# Revit family: Door_Coiling_UltiGroup_Spiral Plus
name_source: partatom
category: Doors
revit_build: Autodesk Revit 2018 (Build: 20170223_1515(x64)
units: mm (PartAtom-declared; Revit-internal decimal feet)

## family parameters
Always vertical = Yes
Cut with Voids When Loaded = No
Host = Wall
OmniClass Number = 23.30.10.17.27.11
OmniClass Title = Overhead Coiling
Room Calculation Point = No
Shared = No

## types (1)
- Type 1
    Analytic Construction = <None>
    Control Box Distance = 150 mm
    Control Box Height = 1200 mm
    Description = Ulti Spiral Plus Door
    Door Bottom Seal = 40 mm  [stored 0.131234 ft]
    Door Seal = Door Seal
    Door open = 0 mm  [stored 0 ft]
    DoorFrameMaterial_ANZRS = Door Frame Material
    DoorGlazingHeight_ANZRS = 0 mm  [stored 0 ft]
    DoorGlazingWidth_ANZRS = 0 mm  [stored 0 ft]
    DoorGrilleHeight_ANZRS = 0 mm  [stored 0 ft]
    DoorGrilleWidth_ANZRS = 0 mm  [stored 0 ft]
    DoorGrille_ANZRS = No
    DoorNumberOfPanels_ANZRS = 0
    DoorOperation_ANZRS = Large heavy duty mushroom head push button, push button and emergency stop button fitted to control box
    DoorPanelBWidth_ANZRS = 0 mm  [stored 0 ft]
    DoorPanelDepth_ANZRS = 0 mm  [stored 0 ft]
    DoorPanelFinish_ANZRS = 50mm Dual wall aluminium insulated slats
    DoorPanelHeight_ANZRS = 0 mm  [stored 0 ft]
    DoorPanelMaterial_ANZRS = Door Panel Material
    DoorPanelWidth_ANZRS = 0 mm  [stored 0 ft]
    Fax = 07 846 2467
    Function = Interior
    Headroom = 850 mm  [stored 2.78871 ft]
    Height = 4000 mm  [stored 13.1234 ft]
    InstallationGroup_ANZRS = 0
    Manufacturer = Ulti Group Ltd.
    Model = Ulti Spiral Plus Door
    ModifiedIssue_ANZRS = 0 $
    Overhead Hood width = 4232 mm  [stored 13.8845 ft]
    Send Message = http://ultigroup.co.nz
    URL = www.ultigroup.co.nz
    Wall Closure = By host
    Width = 4000 mm  [stored 13.1234 ft]

note: [stored X ft] marks values corroborated as IEEE doubles in the binary element streams (Revit-internal decimal feet)

## geometry (parser evidence)
native form markers: Blend x2, Sweep x27
no freeform markers — native parametric forms only
